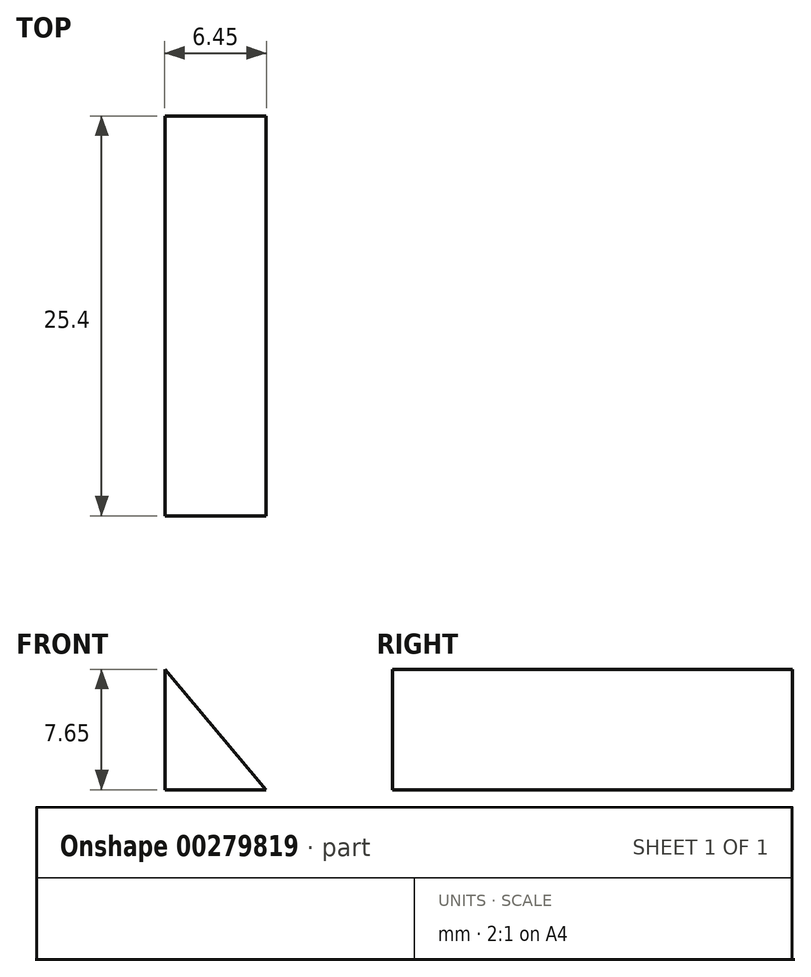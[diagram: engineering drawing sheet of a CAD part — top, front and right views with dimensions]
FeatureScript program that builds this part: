
annotation { "Feature Type Name" : "Feature", "Feature Type Description" : "" }
export const myFeature = defineFeature(function(context is Context, id is Id, definition is map)
    precondition{}
    {
        {
            var Q0;
            Q0=qCreatedBy(makeId("Front.planeOp"),FACE);
            var sketch = newSketch(context, id + "F0", { "sketchPlane" : qUnion([Q0])});
            skLineSegment(sketch, "E0", {"start": v(-44.1, 48.47) * mm, "end": v(-44.1, 40.82) * mm});
            skLineSegment(sketch, "E1", {"start": v(-44.1, 40.82) * mm, "end": v(-37.66, 40.82) * mm});
            skLineSegment(sketch, "E2", {"start": v(-37.66, 40.82) * mm, "end": v(-44.1, 48.47) * mm});
            skSolve(sketch);
        }
        {
            var Q0;
            Q0 = qSketchRegion(id + "F0", true);
            extrude(context, id + "F1", {"entities" : qUnion([Q0]), "depth" : 25.4 * mm});
        }
    });
